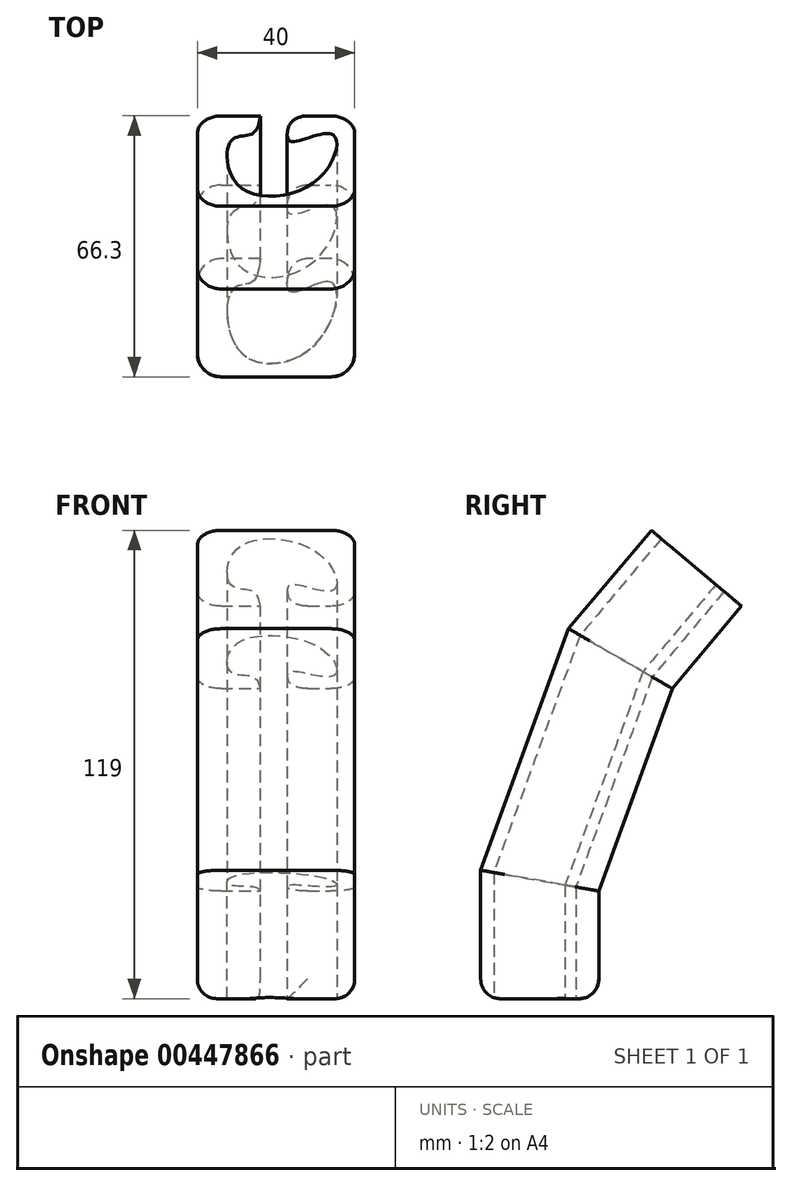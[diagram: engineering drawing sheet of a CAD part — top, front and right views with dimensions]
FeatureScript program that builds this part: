
annotation { "Feature Type Name" : "Feature", "Feature Type Description" : "" }
export const myFeature = defineFeature(function(context is Context, id is Id, definition is map)
    precondition{}
    {
        {
            var Q0;
            Q0=qCreatedBy(makeId("Top.planeOp"),FACE);
            var sketch = newSketch(context, id + "F0", { "sketchPlane" : qUnion([Q0])});
            skLineSegment(sketch, "E0.bottom", {"start": v(-14, 15) * mm, "end": v(-4, 15) * mm});
            skLineSegment(sketch, "E0.top", {"start": v(-14, -15) * mm, "end": v(14, -15) * mm});
            skLineSegment(sketch, "E0.left", {"start": v(-20, 9) * mm, "end": v(-20, -9) * mm});
            skLineSegment(sketch, "E0.right", {"start": v(20, 9) * mm, "end": v(20, -9) * mm});
            skPoint(sketch, "E0.middle", {"position": v(0, 0) * mm});
            skPoint(sketch, "E1", {"position": v(-4, 15) * mm});
            skPoint(sketch, "E2", {"position": v(4, 15) * mm});
            skPoint(sketch, "E3", {"position": v(-14, 15) * mm});
            skPoint(sketch, "E4", {"position": v(-20, 9) * mm});
            skArc(sketch, "E5", {"start": v(-14, 15) * mm, "mid": v(-18.24, 13.24) * mm, "end": v(-20, 9) * mm});
            skPoint(sketch, "E6.orphan", {"position": v(-20, 15) * mm});
            skPoint(sketch, "E7.MirrorP", {"position": v(20, 15) * mm});
            skArc(sketch, "E8.MirrorCS", {"start": v(14, 15) * mm, "mid": v(18.24, 13.24) * mm, "end": v(20, 9) * mm});
            skPoint(sketch, "E9.MirrorP", {"position": v(14, 15) * mm});
            skPoint(sketch, "E10.MirrorP", {"position": v(20, 9) * mm});
            skPoint(sketch, "E11.MirrorP", {"position": v(-20, -9) * mm});
            skPoint(sketch, "E12.MirrorP", {"position": v(-14, -15) * mm});
            skPoint(sketch, "E13.visualSharp", {"position": v(-20, -15) * mm});
            skArc(sketch, "E13.filletArc", {"start": v(-20, -9) * mm, "mid": v(-18.24, -13.24) * mm, "end": v(-14, -15) * mm});
            skArc(sketch, "E14.MirrorCS", {"start": v(14, -15) * mm, "mid": v(18.24, -13.24) * mm, "end": v(20, -9) * mm});
            skPoint(sketch, "E15.orphan", {"position": v(20, -15) * mm});
            skFitSpline(sketch, "E16", {"points": [v(-4, 15) * mm, v(-6.17, 9) * mm, v(-11.05, 7.16) * mm, v(-8.8, -8.92) * mm, v(10.3, -6.4) * mm, v(14, 9) * mm, v(4, 6.5) * mm, v(4, 15) * mm], "startDerivative": vector(-4.25, -69.3) * mm, "endDerivative": vector(26.49, 102.5) * mm});
            skLineSegment(sketch, "E17.trimOffspring", {"start": v(4, 15) * mm, "end": v(14, 15) * mm});
            skSolve(sketch);
        }
        {
            var Q0;
            Q0=qCreatedBy(makeId("Right.planeOp"),FACE);
            var sketch = newSketch(context, id + "F1", { "sketchPlane" : qUnion([Q0])});
            skPoint(sketch, "E18", {"position": v(0, 0) * mm});
            skLineSegment(sketch, "E19", {"start": v(0, 0) * mm, "end": v(0, 30) * mm});
            skLineSegment(sketch, "E20.MirrorCS", {"start": v(0, 30) * mm, "end": v(20.52, 86.38) * mm});
            skLineSegment(sketch, "E21.MirrorCS", {"start": v(20.52, 86.38) * mm, "end": v(39.8, 109.36) * mm});
            skSolve(sketch);
        }
        {
            var Q0;
            Q0 = qSketchRegion(id + "F0", true);
            var Q1;
            Q1 = qConstructionFilter(qBodyType(qCreatedBy(id + "F1" ,EDGE), BodyType.WIRE), ConstructionObject.NO);
            sweep(context, id + "F2", {"profiles" : qUnion([Q0]), "path" : qUnion([Q1])});
        }
        {
            var Q0;
            Q0=makeQuery(id+"F2.opSweep","SWEPT_EDGE",EDGE,{"disambiguationData":[OSD([sQuery(id+"F0.wireOp",EDGE,"E16"),sQuery(id+"F0.wireOp",EDGE,"E17.trimOffspring"),sQuery(id+"F1.wireOp",EDGE,"E20.MirrorCS")])]});
            var Q1;
            Q1=makeQuery(id+"F2.opSweep","SWEPT_EDGE",EDGE,{"disambiguationData":[OSD([sQuery(id+"F0.wireOp",EDGE,"E16"),sQuery(id+"F0.wireOp",EDGE,"E17.trimOffspring"),sQuery(id+"F1.wireOp",EDGE,"E21.MirrorCS")])]});
            var Q2;
            Q2=makeQuery(id+"F2.opSweep","SWEPT_EDGE",EDGE,{"disambiguationData":[OSD([sQuery(id+"F0.wireOp",EDGE,"E16"),sQuery(id+"F0.wireOp",EDGE,"E17.trimOffspring"),sQuery(id+"F1.wireOp",EDGE,"E19")])]});
            var Q3;
            Q3=makeQuery(id+"F2.opSweep","CAP_EDGE",EDGE,{"disambiguationData":[OSD([sQuery(id+"F0.wireOp",EDGE,"E17.trimOffspring"),sQuery(id+"F1.wireOp",VERTEX,"E19.start")])],"isStart":true});
            fillet(context, id + "F3", {"entities" : qUnion([Q0, Q1, Q2, Q3]), "radius" : 5 * mm, "tangentPropagation" : true, "allowEdgeOverflow" : false});
        }
    });
